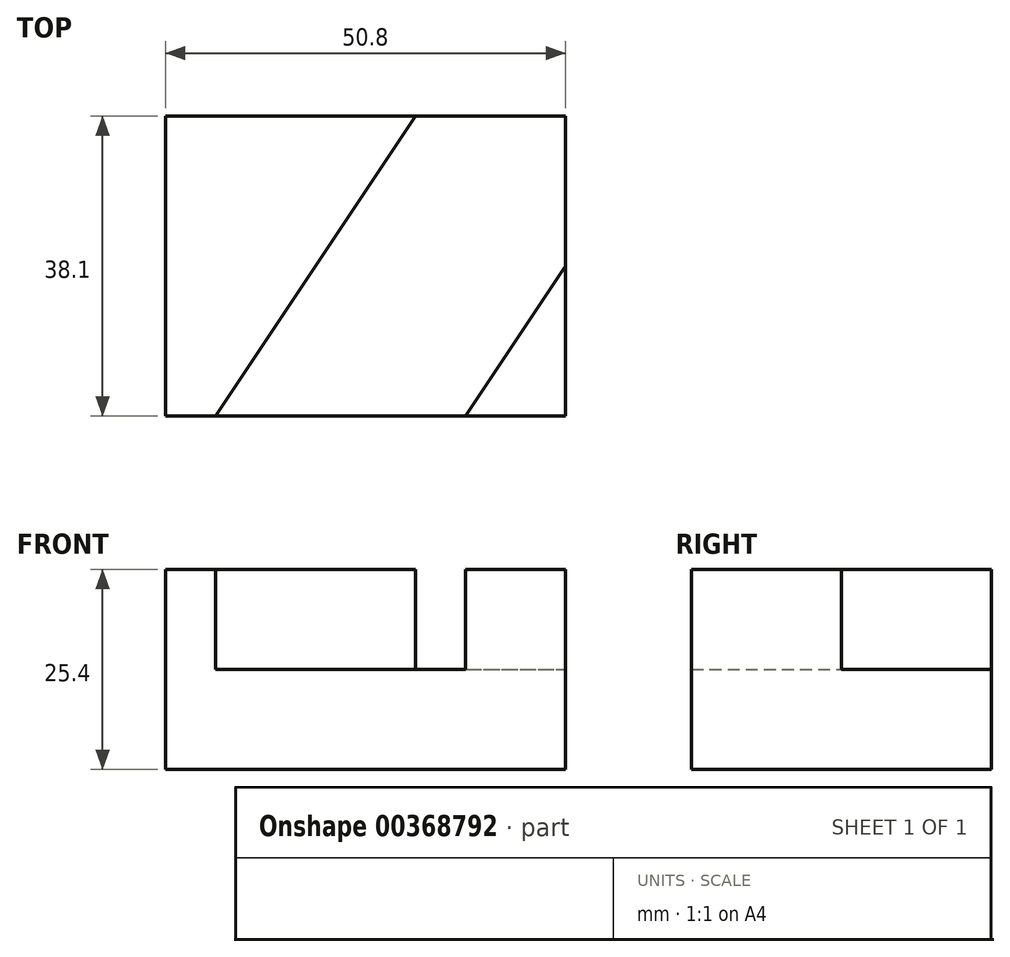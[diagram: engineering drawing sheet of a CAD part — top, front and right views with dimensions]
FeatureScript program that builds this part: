
annotation { "Feature Type Name" : "Feature", "Feature Type Description" : "" }
export const myFeature = defineFeature(function(context is Context, id is Id, definition is map)
    precondition{}
    {
        {
            var Q0;
            Q0=qCreatedBy(makeId("Top.planeOp"),FACE);
            var sketch = newSketch(context, id + "F0", { "sketchPlane" : qUnion([Q0])});
            skLineSegment(sketch, "E0.bottom", {"start": v(-20.89, 33.67) * mm, "end": v(29.91, 33.67) * mm});
            skLineSegment(sketch, "E0.top", {"start": v(-20.89, -4.43) * mm, "end": v(29.91, -4.43) * mm});
            skLineSegment(sketch, "E0.left", {"start": v(-20.89, 33.67) * mm, "end": v(-20.89, -4.43) * mm});
            skLineSegment(sketch, "E0.right", {"start": v(29.91, 33.67) * mm, "end": v(29.91, -4.43) * mm});
            skSolve(sketch);
        }
        {
            var Q0;
            Q0 = qSketchRegion(id + "F0", true);
            extrude(context, id + "F1", {"entities" : qUnion([Q0]), "depth" : 12.7 * mm});
        }
        {
            var Q0;
            Q0=makeQuery(id+"F1.opExtrude","CAP_FACE",FACE,{"disambiguationData":[OSD([sQuery(id+"F0.wireOp",EDGE,"E0.bottom"),sQuery(id+"F0.wireOp",EDGE,"E0.top"),sQuery(id+"F0.wireOp",EDGE,"E0.left"),sQuery(id+"F0.wireOp",EDGE,"E0.right")])],"isStart":false});
            var sketch = newSketch(context, id + "F2", { "sketchPlane" : qUnion([Q0])});
            skLineSegment(sketch, "E1", {"start": v(29.91, -4.43) * mm, "end": v(17.21, -4.43) * mm});
            skLineSegment(sketch, "E2", {"start": v(17.21, -4.43) * mm, "end": v(29.91, 14.62) * mm});
            skLineSegment(sketch, "E3", {"start": v(29.91, 14.62) * mm, "end": v(29.91, -4.43) * mm});
            skLineSegment(sketch, "E4", {"start": v(-20.89, -4.43) * mm, "end": v(-14.54, -4.43) * mm});
            skLineSegment(sketch, "E5", {"start": v(-14.54, -4.43) * mm, "end": v(10.86, 33.67) * mm});
            skLineSegment(sketch, "E6", {"start": v(10.86, 33.67) * mm, "end": v(-20.89, 33.67) * mm});
            skLineSegment(sketch, "E7", {"start": v(-20.89, 33.67) * mm, "end": v(-20.89, -4.43) * mm});
            skSolve(sketch);
        }
        {
            var Q0;
            Q0 = qSketchRegion(id + "F2", true);
            extrude(context, id + "F3", {"entities" : qUnion([Q0]), "operationType" : NewBodyOperationType.ADD, "depth" : 12.7 * mm});
        }
    });
